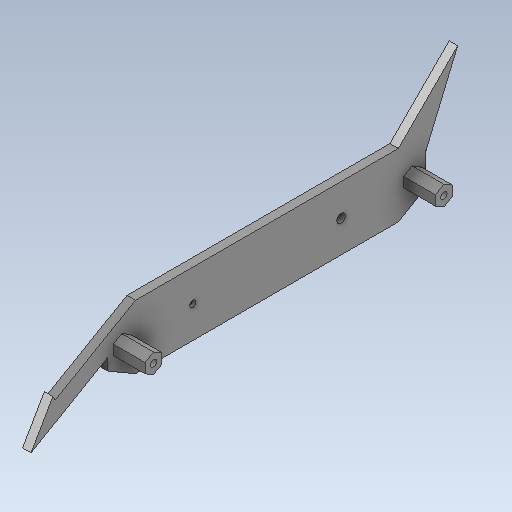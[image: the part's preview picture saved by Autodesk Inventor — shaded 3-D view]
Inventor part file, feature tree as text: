
AUTODESK INVENTOR PART (.ipt)
format: ipt  version: 2020 (Build 240168000, 168)  size: 176,640 bytes
history: native  units: in
note: dims shown in document units (in); Inventor stores cm internally (conversion verified against a paired STEP export)
features: other x3, extrude x2, sketch x2
ambient origin geometry x8: Origin, YZ Plane, XZ Plane, XY Plane, X Axis, Y Axis, Z Axis, Center Point
bodies: Solid1 (feature_tree)
feature tree (7):
  other  "HexWheelGuard.ipt"
  extrude  "Extrusion1"  TaperAngle=0.0deg  [1 undecoded]
  extrude  "Extrusion2"  Depth=0.5906in
  other  "Solid1::HexWheelGuard.ipt"
  other  "TaggingFeature1"
  sketch  "Sketch1"  dims[d0=0.3937in d6=0.0in d7=0.0in]
  sketch  "Sketch2"  dims[d9=0.315in d10=1.4843in d11=60.0deg d12=0.0787in d13=0.3937in d14=0.0in d20=0.3937in d21=0.5906in d22=1.1024in]
note: 1 required parameter value undecoded (feature->parameter linkage not recoverable at this tier; creation-order binding heuristic only, values carry confidence <= 0.55)
